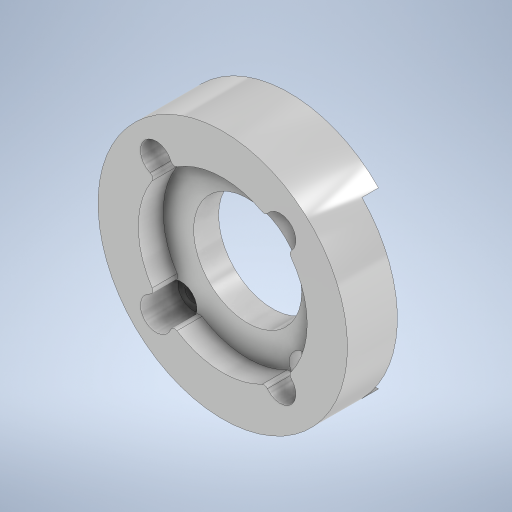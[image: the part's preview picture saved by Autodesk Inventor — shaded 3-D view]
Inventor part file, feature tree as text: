
AUTODESK INVENTOR PART (.ipt)
format: ipt  version: 2024.2 (Build 282272000, 272)  size: 335,872 bytes
history: native  units: in
note: dims shown in document units (in); Inventor stores cm internally (conversion verified against a paired STEP export)
features: sketch x6, extrude x5, hole x1, fillet x1
ambient origin geometry x8: Origin, YZ Plane, XZ Plane, XY Plane, X Axis, Y Axis, Z Axis, Center Point
bodies: Body1 (feature_tree)
feature tree (13):
  extrude  "Extrusion7"  Depth=0.315in TaperAngle=0.0deg
  extrude  "Extrusion8"  Depth=0.0787in TaperAngle=0.0deg
  extrude  "Extrusion9"  Depth=0.1181in TaperAngle=0.0deg
  extrude  "Extrusion11"  Depth=0.315in
  hole  "Hole2"  [1 undecoded]
  extrude  "Extrusion12"  Depth=0.0157in
  fillet  "Fillet2"  [1 undecoded]
  sketch  "Sketch8"  dims[d33=1.1811in d34=0.315in d35=0.0in]
  sketch  "Sketch10"  dims[d37=0.0787in d38=0.0in d39=0.0433in d40=0.0in]
  sketch  "Sketch11"  dims[d44=0.0079in d45=0.1181in d46=0.0in]
  sketch  "Sketch13"  dims[d47=0.0827in d48=0.2362in d49=0.1575in d50=0.0787in d51=90.0deg d52=0.315in d53=0.8108in d54=0.1496in]
  sketch  "Sketch14"  dims[d55=0.1772in d56=0.0in d57=0.0197in]
  sketch  "Sketch15"  dims[d58=0.5118in d59=0.0157in]
note: 2 required parameter values undecoded (feature->parameter linkage not recoverable at this tier; creation-order binding heuristic only, values carry confidence <= 0.55)
